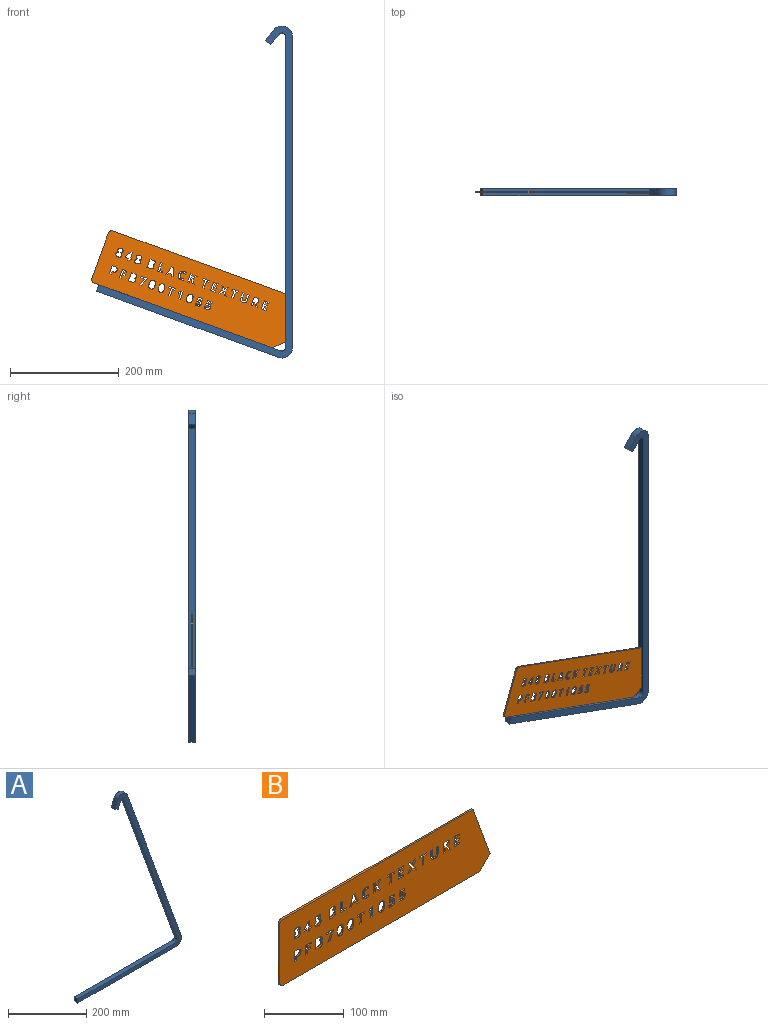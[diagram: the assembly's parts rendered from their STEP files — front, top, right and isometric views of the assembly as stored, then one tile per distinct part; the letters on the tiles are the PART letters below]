
ASSEMBLY  parts=2 mates=1
PART A: 14 faces, bbox 374.7x12.7x575.1 mm
  f0: plane 12.7x12.7mm, normal (-1,0,0), area 161.3mm2, adj f2,f3,f4,f5
  f1: plane 12.7x11.93mm, normal (-0.34,0,-0.94), area 161.3mm2, adj f3,f5,f12,f13
  f2: plane 355.6x12.7mm, normal (0,0,1), area 4516.1mm2, adj f0,f3,f5,f6
  f3: plane 575.13x374.65mm, normal (0,-1,0), area 12800.5mm2, adj f0,f1,f2,f4,f6,f7,f8,f9
  f4: plane 355.6x12.7mm, normal (0,0,-1), area 4516.1mm2, adj f0,f3,f5,f7
  f5: plane 575.13x374.65mm, normal (0,1,0), area 12800.5mm2, adj f0,f1,f2,f4,f6,f7,f8,f9
  f6: cylinder r=6.35mm len=12.7mm, axis (0,-1,0), area 154.8mm2, adj f2,f3,f5,f8
  f7: cylinder r=19.05mm len=25.57mm, axis (0,-1,0), area 464.5mm2, adj f3,f4,f5,f9
  f8: plane 537.03x195.46mm, normal (-0.94,0,-0.34), area 7258.1mm2, adj f3,f5,f6,f10
  f9: plane 537.03x195.46mm, normal (0.94,0,0.34), area 7258mm2, adj f3,f5,f7,f11
  f10: cylinder r=6.35mm len=12.7mm, axis (0,-1,0), area 197.1mm2, adj f3,f5,f8,f12
  f11: cylinder r=19.05mm len=35.8mm, axis (0,-1,0), area 591.2mm2, adj f3,f5,f9,f13
  f12: plane 23.87x12.7mm, normal (0.94,0,-0.34), area 322.6mm2, adj f1,f3,f5,f10
  f13: plane 23.87x12.7mm, normal (-0.94,0,0.34), area 322.6mm2, adj f1,f3,f5,f11
PART B: 305 faces, bbox 374.2x2.7x101.6 mm
  f0: plane 374.22x101.6mm, normal (0,-1,0), area 33695.3mm2, adj f1,f3,f4,f5,f6,f7,f8,f9
  f1: plane 337.67x2.74mm, normal (0,0,1), area 926.3mm2, adj f0,f2,f301,f303
  f2: plane 374.22x101.6mm, normal (0,1,0), area 33695.3mm2, adj f1,f3,f4,f5,f6,f7,f8,f9
  f3: plane 349.25x2.74mm, normal (0,0,-1), area 958.1mm2, adj f0,f2,f302,f304
  f4: plane 88.9x2.74mm, normal (-1,0,0), area 243.9mm2, adj f0,f2,f303,f304
  f5: plane 15.74x2.74mm, normal (1,0,0), area 43.2mm2, adj f0,f2,f6,f10
  f6: plane 9.72x2.74mm, normal (0,0,1), area 26.7mm2, adj f0,f2,f5,f7
  f7: plane 2.76x2.74mm, normal (-1,0,0), area 7.6mm2, adj f0,f2,f6,f8
  f8: plane 6.38x2.74mm, normal (0,0,-1), area 17.5mm2, adj f0,f2,f7,f9
  f9: plane 12.98x2.74mm, normal (-1,0,0), area 35.6mm2, adj f0,f2,f8,f10
  f10: plane 3.34x2.74mm, normal (0,0,-1), area 9.2mm2, adj f0,f2,f5,f9
  f11: extruded ~6.1x2.74mm, area 17.4mm2, adj f0,f2,f12,f18
  f12: extruded ~6.05x2.74mm, area 17.3mm2, adj f0,f2,f11,f13
  f13: extruded ~4.12x2.74mm, area 13.2mm2, adj f0,f2,f12,f14
  f14: extruded ~4.14x2.74mm, area 13.2mm2, adj f0,f2,f13,f15
  f15: extruded ~6.14x2.74mm, area 17.5mm2, adj f0,f2,f14,f16
  f16: extruded ~6.04x2.74mm, area 17.2mm2, adj f0,f2,f15,f17
  f17: extruded ~4.11x2.74mm, area 13.2mm2, adj f0,f2,f16,f18
  f18: extruded ~4.16x2.74mm, area 13.2mm2, adj f0,f2,f11,f17
  f19: extruded ~2.77x2.74mm, area 8.8mm2, adj f0,f2,f20,f34
  f20: extruded ~2.74x2.15mm, area 6.3mm2, adj f0,f2,f19,f21
  f21: extruded ~2.74x2.15mm, area 7.6mm2, adj f0,f2,f20,f22
  f22: extruded ~2.74x2.53mm, area 8.9mm2, adj f0,f2,f21,f23
  f23: extruded ~2.74x2.26mm, area 6.7mm2, adj f0,f2,f22,f24
  f24: extruded ~3.12x2.74mm, area 9.9mm2, adj f0,f2,f23,f25
  f25: extruded ~3.99x2.74mm, area 11.6mm2, adj f0,f2,f24,f26
  f26: extruded ~4.06x2.74mm, area 11.7mm2, adj f0,f2,f25,f27
  f27: extruded ~3.11x2.74mm, area 9.8mm2, adj f0,f2,f26,f28
  f28: extruded ~2.74x2.39mm, area 7mm2, adj f0,f2,f27,f29
  f29: extruded ~2.74x2.3mm, area 8.2mm2, adj f0,f2,f28,f30
  f30: extruded ~2.74x1.94mm, area 7.4mm2, adj f0,f2,f29,f31
  f31: extruded ~2.74x2.12mm, area 6.1mm2, adj f0,f2,f30,f32
  f32: extruded ~2.74x2.74mm, area 8.8mm2, adj f0,f2,f31,f33
  f33: extruded ~3.65x2.74mm, area 10.6mm2, adj f0,f2,f32,f34
  f34: extruded ~3.65x2.74mm, area 10.6mm2, adj f0,f2,f19,f33
  f35: extruded ~2.77x2.74mm, area 8.8mm2, adj f0,f2,f36,f50
  f36: extruded ~2.74x2.15mm, area 6.3mm2, adj f0,f2,f35,f37
  f37: extruded ~2.74x2.15mm, area 7.6mm2, adj f0,f2,f36,f38
  f38: extruded ~2.74x2.53mm, area 8.9mm2, adj f0,f2,f37,f39
  f39: extruded ~2.74x2.26mm, area 6.7mm2, adj f0,f2,f38,f40
  f40: extruded ~3.12x2.74mm, area 9.9mm2, adj f0,f2,f39,f41
  f41: extruded ~3.99x2.74mm, area 11.6mm2, adj f0,f2,f40,f42
  f42: extruded ~4.06x2.74mm, area 11.7mm2, adj f0,f2,f41,f43
  f43: extruded ~3.11x2.74mm, area 9.8mm2, adj f0,f2,f42,f44
  f44: extruded ~2.74x2.39mm, area 7mm2, adj f0,f2,f43,f45
  f45: extruded ~2.74x2.3mm, area 8.2mm2, adj f0,f2,f44,f46
  f46: extruded ~2.74x1.94mm, area 7.4mm2, adj f0,f2,f45,f47
  f47: extruded ~2.74x2.12mm, area 6.1mm2, adj f0,f2,f46,f48
  f48: extruded ~2.74x2.74mm, area 8.8mm2, adj f0,f2,f47,f49
  f49: extruded ~3.65x2.74mm, area 10.6mm2, adj f0,f2,f48,f50
  f50: extruded ~3.65x2.74mm, area 10.6mm2, adj f0,f2,f35,f49
  f51: extruded ~4.86x2.74mm, area 13.7mm2, adj f0,f2,f52,f62
  f52: extruded ~3.03x2.74mm, area 9.7mm2, adj f0,f2,f51,f53
  f53: extruded ~2.74x2.32mm, area 6.7mm2, adj f0,f2,f52,f54
  f54: extruded ~2.74x1.76mm, area 5.8mm2, adj f0,f2,f53,f55
  f55: plane 2.74x0.11mm, normal (-1,0,0), area 0.3mm2, adj f0,f2,f54,f56
  f56: extruded ~2.74x2.16mm, area 7mm2, adj f0,f2,f55,f57
  f57: extruded ~2.74x2.43mm, area 7mm2, adj f0,f2,f56,f58
  f58: extruded ~3.36x2.74mm, area 10.5mm2, adj f0,f2,f57,f59
  f59: extruded ~4.23x2.74mm, area 12.3mm2, adj f0,f2,f58,f60
  f60: plane 5.89x2.74mm, normal (0,0,1), area 16.2mm2, adj f0,f2,f59,f61
  f61: plane 15.74x2.74mm, normal (1,0,0), area 43.2mm2, adj f0,f2,f60,f62
  f62: plane 4.9x2.74mm, normal (0,0,-1), area 13.4mm2, adj f0,f2,f51,f61
  f63: plane 3.34x2.74mm, normal (0,0,1), area 9.2mm2, adj f0,f2,f64,f74
  f64: plane 15.74x2.74mm, normal (1,0,0), area 43.2mm2, adj f0,f2,f63,f65
  f65: plane 4.59x2.74mm, normal (0,0,-1), area 12.6mm2, adj f0,f2,f64,f66
  f66: extruded ~4.75x2.74mm, area 13.6mm2, adj f0,f2,f65,f67
  f67: extruded ~3.55x2.74mm, area 11mm2, adj f0,f2,f66,f68
  f68: extruded ~2.74x2.47mm, area 7.2mm2, adj f0,f2,f67,f69
  f69: extruded ~2.74x2.17mm, area 7.6mm2, adj f0,f2,f68,f70
  f70: extruded ~6.86x4.63mm, area 22.7mm2, adj f0,f2,f69,f71
  f71: plane 3.7x2.74mm, normal (0,0,1), area 10.2mm2, adj f0,f2,f70,f72
  f72: plane 6.04x3.76mm, normal (0.85,0,0.53), area 19.5mm2, adj f0,f2,f71,f73
  f73: plane 2.74x1.77mm, normal (0,0,1), area 4.9mm2, adj f0,f2,f72,f74
  f74: plane 6.04x2.74mm, normal (-1,0,0), area 16.6mm2, adj f0,f2,f63,f73
  f75: extruded ~4.52x2.74mm, area 13.2mm2, adj f0,f2,f76,f83
  f76: plane 2.74x1.43mm, normal (0,0,1), area 3.9mm2, adj f0,f2,f75,f77
  f77: plane 5.6x2.74mm, normal (-1,0,0), area 15.4mm2, adj f0,f2,f76,f78
  f78: plane 3.34x2.74mm, normal (0,0,1), area 9.2mm2, adj f0,f2,f77,f79
  f79: plane 15.74x2.74mm, normal (1,0,0), area 43.2mm2, adj f0,f2,f78,f80
  f80: plane 5.03x2.74mm, normal (0,0,-1), area 13.8mm2, adj f0,f2,f79,f81
  f81: extruded ~4.36x2.74mm, area 12.7mm2, adj f0,f2,f80,f82
  f82: extruded ~3.68x2.74mm, area 11.3mm2, adj f0,f2,f81,f83
  f83: extruded ~3.89x2.74mm, area 11.9mm2, adj f0,f2,f75,f82
  f84: extruded ~6.1x2.74mm, area 17.4mm2, adj f0,f2,f85,f91
  f85: extruded ~6.05x2.74mm, area 17.3mm2, adj f0,f2,f84,f86
  f86: extruded ~4.12x2.74mm, area 13.2mm2, adj f0,f2,f85,f87
  f87: extruded ~4.14x2.74mm, area 13.2mm2, adj f0,f2,f86,f88
  f88: extruded ~6.14x2.74mm, area 17.5mm2, adj f0,f2,f87,f89
  f89: extruded ~6.04x2.74mm, area 17.2mm2, adj f0,f2,f88,f90
  f90: extruded ~4.11x2.74mm, area 13.2mm2, adj f0,f2,f89,f91
  f91: extruded ~4.16x2.74mm, area 13.2mm2, adj f0,f2,f84,f90
  f92: extruded ~6.1x2.74mm, area 17.4mm2, adj f0,f2,f93,f99
  f93: extruded ~6.05x2.74mm, area 17.3mm2, adj f0,f2,f92,f94
  f94: extruded ~4.12x2.74mm, area 13.2mm2, adj f0,f2,f93,f95
  f95: extruded ~4.14x2.74mm, area 13.2mm2, adj f0,f2,f94,f96
  f96: extruded ~6.14x2.74mm, area 17.5mm2, adj f0,f2,f95,f97
  f97: extruded ~6.04x2.74mm, area 17.2mm2, adj f0,f2,f96,f98
  f98: extruded ~4.11x2.74mm, area 13.2mm2, adj f0,f2,f97,f99
  f99: extruded ~4.16x2.74mm, area 13.2mm2, adj f0,f2,f92,f98
  f100: extruded ~4.86x2.74mm, area 13.7mm2, adj f0,f2,f101,f111
  f101: extruded ~3.03x2.74mm, area 9.7mm2, adj f0,f2,f100,f102
  f102: extruded ~2.74x2.32mm, area 6.7mm2, adj f0,f2,f101,f103
  f103: extruded ~2.74x1.76mm, area 5.8mm2, adj f0,f2,f102,f104
  f104: plane 2.74x0.11mm, normal (-1,0,0), area 0.3mm2, adj f0,f2,f103,f105
  f105: extruded ~2.74x2.16mm, area 7mm2, adj f0,f2,f104,f106
  f106: extruded ~2.74x2.43mm, area 7mm2, adj f0,f2,f105,f107
  f107: extruded ~3.36x2.74mm, area 10.5mm2, adj f0,f2,f106,f108
  f108: extruded ~4.23x2.74mm, area 12.3mm2, adj f0,f2,f107,f109
  f109: plane 5.89x2.74mm, normal (0,0,1), area 16.2mm2, adj f0,f2,f108,f110
  f110: plane 15.74x2.74mm, normal (1,0,0), area 43.2mm2, adj f0,f2,f109,f111
  f111: plane 4.9x2.74mm, normal (0,0,-1), area 13.4mm2, adj f0,f2,f100,f110
  f112: extruded ~2.92x2.74mm, area 9.3mm2, adj f0,f2,f113,f126
  f113: extruded ~2.74x1.75mm, area 4.9mm2, adj f0,f2,f112,f114
  f114: extruded ~2.74x1.78mm, area 5.3mm2, adj f0,f2,f113,f115
  f115: plane 2.74x2.71mm, normal (-0.93,0,0.37), area 8mm2, adj f0,f2,f114,f116
  f116: extruded ~4.61x2.74mm, area 13.1mm2, adj f0,f2,f115,f117
  f117: extruded ~3.92x2.74mm, area 11.2mm2, adj f0,f2,f116,f118
  f118: extruded ~2.83x2.74mm, area 10.6mm2, adj f0,f2,f117,f119
  f119: extruded ~4.3x2.74mm, area 12.2mm2, adj f0,f2,f118,f120
  f120: extruded ~5.98x2.74mm, area 17.5mm2, adj f0,f2,f119,f121
  f121: extruded ~5.25x2.74mm, area 16mm2, adj f0,f2,f120,f122
  f122: extruded ~4.33x2.74mm, area 12.2mm2, adj f0,f2,f121,f123
  f123: plane 2.8x2.74mm, normal (-1,0,0), area 7.7mm2, adj f0,f2,f122,f124
  f124: extruded ~4.01x2.74mm, area 11.3mm2, adj f0,f2,f123,f125
  f125: extruded ~5.26x3.95mm, area 20.6mm2, adj f0,f2,f124,f126
  f126: extruded ~3.94x2.74mm, area 11.4mm2, adj f0,f2,f112,f125
  f127: plane 3.79x2.74mm, normal (0,0,1), area 10.4mm2, adj f0,f2,f128,f139
  f128: plane 8.77x5.53mm, normal (-0.85,0,-0.53), area 28.5mm2, adj f0,f2,f127,f129
  f129: plane 6.97x5.49mm, normal (-0.79,0,0.62), area 24.3mm2, adj f0,f2,f128,f130
  f130: plane 3.7x2.74mm, normal (0,0,-1), area 10.2mm2, adj f0,f2,f129,f131
  f131: plane 5.35x4.27mm, normal (0.78,0,-0.62), area 18.8mm2, adj f0,f2,f130,f132
  f132: plane 2.74x1.85mm, normal (0.82,0,-0.58), area 6.2mm2, adj f0,f2,f131,f133
  f133: plane 7.2x2.74mm, normal (-1,0,0), area 19.8mm2, adj f0,f2,f132,f134
  f134: plane 3.34x2.74mm, normal (0,0,-1), area 9.2mm2, adj f0,f2,f133,f135
  f135: plane 15.74x2.74mm, normal (1,0,0), area 43.2mm2, adj f0,f2,f134,f136
  f136: plane 3.34x2.74mm, normal (0,0,1), area 9.2mm2, adj f0,f2,f135,f137
  f137: plane 5.62x2.74mm, normal (-1,0,0), area 15.4mm2, adj f0,f2,f136,f138
  f138: plane 2.74x1.41mm, normal (-0.58,0,0.81), area 4.8mm2, adj f0,f2,f137,f139
  f139: plane 6.63x4.12mm, normal (0.85,0,0.53), area 21.4mm2, adj f0,f2,f127,f138
  f140: plane 3.34x2.74mm, normal (0,0,1), area 9.2mm2, adj f0,f2,f141,f147
  f141: plane 12.96x2.74mm, normal (-1,0,0), area 35.6mm2, adj f0,f2,f140,f142
  f142: plane 4.27x2.74mm, normal (0,0,1), area 11.7mm2, adj f0,f2,f141,f143
  f143: plane 2.78x2.74mm, normal (-1,0,0), area 7.6mm2, adj f0,f2,f142,f144
  f144: plane 11.89x2.74mm, normal (0,0,-1), area 32.6mm2, adj f0,f2,f143,f145
  f145: plane 2.78x2.74mm, normal (1,0,0), area 7.6mm2, adj f0,f2,f144,f146
  f146: plane 4.28x2.74mm, normal (0,0,1), area 11.7mm2, adj f0,f2,f145,f147
  f147: plane 12.96x2.74mm, normal (1,0,0), area 35.6mm2, adj f0,f2,f140,f146
  f148: plane 9.06x2.74mm, normal (0,0,1), area 24.9mm2, adj f0,f2,f149,f159
  f149: plane 2.76x2.74mm, normal (-1,0,0), area 7.6mm2, adj f0,f2,f148,f150
  f150: plane 5.73x2.74mm, normal (0,0,-1), area 15.7mm2, adj f0,f2,f149,f151
  f151: plane 4.06x2.74mm, normal (-1,0,0), area 11.1mm2, adj f0,f2,f150,f152
  f152: plane 5.33x2.74mm, normal (0,0,1), area 14.6mm2, adj f0,f2,f151,f153
  f153: plane 2.74x2.74mm, normal (-1,0,0), area 7.5mm2, adj f0,f2,f152,f154
  f154: plane 5.33x2.74mm, normal (0,0,-1), area 14.6mm2, adj f0,f2,f153,f155
  f155: plane 3.46x2.74mm, normal (-1,0,0), area 9.5mm2, adj f0,f2,f154,f156
  f156: plane 5.73x2.74mm, normal (0,0,1), area 15.7mm2, adj f0,f2,f155,f157
  f157: plane 2.74x2.74mm, normal (-1,0,0), area 7.5mm2, adj f0,f2,f156,f158
  f158: plane 9.06x2.74mm, normal (0,0,-1), area 24.9mm2, adj f0,f2,f157,f159
  f159: plane 15.74x2.74mm, normal (1,0,0), area 43.2mm2, adj f0,f2,f148,f158
  f160: plane 3.81x2.74mm, normal (0,0,1), area 10.5mm2, adj f0,f2,f161,f171
  f161: plane 7.93x5.32mm, normal (-0.83,0,-0.56), area 26.2mm2, adj f0,f2,f160,f162
  f162: plane 7.81x4.94mm, normal (-0.85,0,0.53), area 25.3mm2, adj f0,f2,f161,f163
  f163: plane 3.59x2.74mm, normal (0,0,-1), area 9.9mm2, adj f0,f2,f162,f164
  f164: plane 5.66x3.33mm, normal (0.86,0,-0.51), area 18mm2, adj f0,f2,f163,f165
  f165: plane 5.66x3.39mm, normal (-0.86,0,-0.51), area 18.1mm2, adj f0,f2,f164,f166
  f166: plane 3.68x2.74mm, normal (0,0,-1), area 10.1mm2, adj f0,f2,f165,f167
  f167: plane 7.62x4.89mm, normal (0.84,0,0.54), area 24.8mm2, adj f0,f2,f166,f168
  f168: plane 8.12x5.22mm, normal (0.84,0,-0.54), area 26.5mm2, adj f0,f2,f167,f169
  f169: plane 3.58x2.74mm, normal (0,0,1), area 9.8mm2, adj f0,f2,f168,f170
  f170: plane 5.95x3.66mm, normal (-0.85,0,0.52), area 19.2mm2, adj f0,f2,f169,f171
  f171: plane 5.95x3.66mm, normal (0.85,0,0.52), area 19.2mm2, adj f0,f2,f160,f170
  f172: plane 3.34x2.74mm, normal (0,0,1), area 9.2mm2, adj f0,f2,f173,f179
  f173: plane 12.96x2.74mm, normal (-1,0,0), area 35.6mm2, adj f0,f2,f172,f174
  f174: plane 4.27x2.74mm, normal (0,0,1), area 11.7mm2, adj f0,f2,f173,f175
  f175: plane 2.78x2.74mm, normal (-1,0,0), area 7.6mm2, adj f0,f2,f174,f176
  f176: plane 11.89x2.74mm, normal (0,0,-1), area 32.6mm2, adj f0,f2,f175,f177
  f177: plane 2.78x2.74mm, normal (1,0,0), area 7.6mm2, adj f0,f2,f176,f178
  f178: plane 4.28x2.74mm, normal (0,0,1), area 11.7mm2, adj f0,f2,f177,f179
  f179: plane 12.96x2.74mm, normal (1,0,0), area 35.6mm2, adj f0,f2,f172,f178
  f180: plane 10.18x2.74mm, normal (-1,0,0), area 27.9mm2, adj f0,f2,f181,f194
  f181: plane 3.33x2.74mm, normal (0,0,-1), area 9.1mm2, adj f0,f2,f180,f182
  f182: plane 9.62x2.74mm, normal (1,0,0), area 26.4mm2, adj f0,f2,f181,f183
  f183: extruded ~2.74x2.69mm, area 7.8mm2, adj f0,f2,f182,f184
  f184: extruded ~2.74x2.37mm, area 7.1mm2, adj f0,f2,f183,f185
  f185: extruded ~2.74x2.42mm, area 7.3mm2, adj f0,f2,f184,f186
  f186: extruded ~2.74x2.67mm, area 7.8mm2, adj f0,f2,f185,f187
  f187: plane 9.64x2.74mm, normal (-1,0,0), area 26.4mm2, adj f0,f2,f186,f188
  f188: plane 3.32x2.74mm, normal (0,0,-1), area 9.1mm2, adj f0,f2,f187,f189
  f189: plane 10.14x2.74mm, normal (1,0,0), area 27.8mm2, adj f0,f2,f188,f190
  f190: extruded ~4.26x2.74mm, area 12.9mm2, adj f0,f2,f189,f191
  f191: extruded ~4.71x2.74mm, area 14mm2, adj f0,f2,f190,f192
  f192: extruded ~3.49x2.74mm, area 9.8mm2, adj f0,f2,f191,f193
  f193: extruded ~2.74x2.26mm, area 8.4mm2, adj f0,f2,f192,f194
  f194: extruded ~3.06x2.74mm, area 8.8mm2, adj f0,f2,f180,f193
  f195: plane 9.06x2.74mm, normal (0,0,1), area 24.9mm2, adj f0,f2,f196,f206
  f196: plane 2.76x2.74mm, normal (-1,0,0), area 7.6mm2, adj f0,f2,f195,f197
  f197: plane 5.73x2.74mm, normal (0,0,-1), area 15.7mm2, adj f0,f2,f196,f198
  f198: plane 4.06x2.74mm, normal (-1,0,0), area 11.1mm2, adj f0,f2,f197,f199
  f199: plane 5.33x2.74mm, normal (0,0,1), area 14.6mm2, adj f0,f2,f198,f200
  f200: plane 2.74x2.74mm, normal (-1,0,0), area 7.5mm2, adj f0,f2,f199,f201
  f201: plane 5.33x2.74mm, normal (0,0,-1), area 14.6mm2, adj f0,f2,f200,f202
  f202: plane 3.46x2.74mm, normal (-1,0,0), area 9.5mm2, adj f0,f2,f201,f203
  f203: plane 5.73x2.74mm, normal (0,0,1), area 15.7mm2, adj f0,f2,f202,f204
  f204: plane 2.74x2.74mm, normal (-1,0,0), area 7.5mm2, adj f0,f2,f203,f205
  f205: plane 9.06x2.74mm, normal (0,0,-1), area 24.9mm2, adj f0,f2,f204,f206
  f206: plane 15.74x2.74mm, normal (1,0,0), area 43.2mm2, adj f0,f2,f195,f205
  f207: plane 3.75x2.74mm, normal (0.96,0,0.29), area 10.7mm2, adj f0,f2,f208,f214
  f208: plane 3.6x2.74mm, normal (0,0,1), area 9.9mm2, adj f0,f2,f207,f209
  f209: plane 15.81x5.58mm, normal (-0.94,0,-0.33), area 46mm2, adj f0,f2,f208,f210
  f210: plane 4.08x2.74mm, normal (0,0,-1), area 11.2mm2, adj f0,f2,f209,f211
  f211: plane 15.81x5.56mm, normal (0.94,0,-0.33), area 46mm2, adj f0,f2,f210,f212
  f212: plane 3.6x2.74mm, normal (0,0,1), area 9.9mm2, adj f0,f2,f211,f213
  f213: plane 3.75x2.74mm, normal (-0.96,0,0.29), area 10.7mm2, adj f0,f2,f212,f214
  f214: plane 5.74x2.74mm, normal (0,0,1), area 15.7mm2, adj f0,f2,f207,f213
  f215: plane 2.74x1.9mm, normal (0,0,1), area 5.2mm2, adj f0,f2,f216,f225
  f216: plane 2.74x2.58mm, normal (-1,0,0), area 7.1mm2, adj f0,f2,f215,f217
  f217: plane 2.74x1.9mm, normal (0,0,-1), area 5.2mm2, adj f0,f2,f216,f218
  f218: plane 9.89x2.74mm, normal (-1,0,0), area 27.1mm2, adj f0,f2,f217,f219
  f219: plane 3.07x2.74mm, normal (0,0,-1), area 8.4mm2, adj f0,f2,f218,f220
  f220: plane 10.16x6.9mm, normal (0.83,0,-0.56), area 33.7mm2, adj f0,f2,f219,f221
  f221: plane 2.74x2.32mm, normal (1,0,0), area 6.4mm2, adj f0,f2,f220,f222
  f222: plane 6.72x2.74mm, normal (0,0,1), area 18.4mm2, adj f0,f2,f221,f223
  f223: plane 3.26x2.74mm, normal (1,0,0), area 8.9mm2, adj f0,f2,f222,f224
  f224: plane 3.25x2.74mm, normal (0,0,1), area 8.9mm2, adj f0,f2,f223,f225
  f225: plane 3.26x2.74mm, normal (-1,0,0), area 8.9mm2, adj f0,f2,f215,f224
  f226: extruded ~3.63x2.74mm, area 10.8mm2, adj f0,f2,f227,f245
  f227: extruded ~2.74x1.63mm, area 4.5mm2, adj f0,f2,f226,f228
  f228: plane 2.74x0.38mm, normal (0.2,0,-0.98), area 1.1mm2, adj f0,f2,f227,f229
  f229: plane 3.09x2.74mm, normal (-1,0,0.09), area 8.5mm2, adj f0,f2,f228,f230
  f230: plane 5.62x2.74mm, normal (0,0,1), area 15.4mm2, adj f0,f2,f229,f231
  f231: plane 2.82x2.74mm, normal (-1,0,0), area 7.7mm2, adj f0,f2,f230,f232
  f232: plane 8.54x2.74mm, normal (0,0,-1), area 23.4mm2, adj f0,f2,f231,f233
  f233: plane 8.02x2.74mm, normal (1,0,-0.07), area 22.1mm2, adj f0,f2,f232,f234
  f234: plane 2.74x1.33mm, normal (0.47,0,0.88), area 4.1mm2, adj f0,f2,f233,f235
  f235: extruded ~2.74x1.12mm, area 3.1mm2, adj f0,f2,f234,f236
  f236: extruded ~2.74x1.26mm, area 3.5mm2, adj f0,f2,f235,f237
  f237: extruded ~3.16x2.74mm, area 12.4mm2, adj f0,f2,f236,f238
  f238: extruded ~3.05x2.74mm, area 12.4mm2, adj f0,f2,f237,f239
  f239: extruded ~2.74x2.14mm, area 5.9mm2, adj f0,f2,f238,f240
  f240: extruded ~2.74x1.98mm, area 5.8mm2, adj f0,f2,f239,f241
  f241: plane 2.88x2.74mm, normal (1,0,0), area 7.9mm2, adj f0,f2,f240,f242
  f242: extruded ~4.24x2.74mm, area 12mm2, adj f0,f2,f241,f243
  f243: extruded ~4.65x2.74mm, area 13.6mm2, adj f0,f2,f242,f244
  f244: extruded ~4.06x2.74mm, area 12.4mm2, adj f0,f2,f243,f245
  f245: extruded ~3.51x2.74mm, area 10.6mm2, adj f0,f2,f226,f244
  f246: extruded ~3.63x2.74mm, area 10.8mm2, adj f0,f2,f247,f265
  f247: extruded ~2.74x1.63mm, area 4.5mm2, adj f0,f2,f246,f248
  f248: plane 2.74x0.38mm, normal (0.2,0,-0.98), area 1.1mm2, adj f0,f2,f247,f249
  f249: plane 3.09x2.74mm, normal (-1,0,0.09), area 8.5mm2, adj f0,f2,f248,f250
  f250: plane 5.62x2.74mm, normal (0,0,1), area 15.4mm2, adj f0,f2,f249,f251
  f251: plane 2.82x2.74mm, normal (-1,0,0), area 7.7mm2, adj f0,f2,f250,f252
  f252: plane 8.54x2.74mm, normal (0,0,-1), area 23.4mm2, adj f0,f2,f251,f253
  f253: plane 8.02x2.74mm, normal (1,0,-0.07), area 22.1mm2, adj f0,f2,f252,f254
  f254: plane 2.74x1.33mm, normal (0.47,0,0.88), area 4.1mm2, adj f0,f2,f253,f255
  f255: extruded ~2.74x1.12mm, area 3.1mm2, adj f0,f2,f254,f256
  f256: extruded ~2.74x1.26mm, area 3.5mm2, adj f0,f2,f255,f257
  f257: extruded ~3.16x2.74mm, area 12.4mm2, adj f0,f2,f256,f258
  f258: extruded ~3.05x2.74mm, area 12.4mm2, adj f0,f2,f257,f259
  f259: extruded ~2.74x2.14mm, area 5.9mm2, adj f0,f2,f258,f260
  f260: extruded ~2.74x1.98mm, area 5.8mm2, adj f0,f2,f259,f261
  f261: plane 2.88x2.74mm, normal (1,0,0), area 7.9mm2, adj f0,f2,f260,f262
  f262: extruded ~4.24x2.74mm, area 12mm2, adj f0,f2,f261,f263
  f263: extruded ~4.65x2.74mm, area 13.6mm2, adj f0,f2,f262,f264
  f264: extruded ~4.06x2.74mm, area 12.4mm2, adj f0,f2,f263,f265
  f265: extruded ~3.51x2.74mm, area 10.6mm2, adj f0,f2,f246,f264
  f266: plane 3.33x2.74mm, normal (0,0,1), area 9.1mm2, adj f0,f2,f267,f275
  f267: plane 15.74x2.74mm, normal (-1,0,0), area 43.2mm2, adj f0,f2,f266,f268
  f268: plane 2.74x2.74mm, normal (0,0,-1), area 7.5mm2, adj f0,f2,f267,f269
  f269: plane 5.07x4.04mm, normal (0.62,0,-0.78), area 17.8mm2, adj f0,f2,f268,f270
  f270: plane 2.74x2mm, normal (0.78,0,0.63), area 7mm2, adj f0,f2,f269,f271
  f271: plane 2.74x1.81mm, normal (-0.63,0,0.78), area 6.4mm2, adj f0,f2,f270,f272
  f272: extruded ~2.74x1.15mm, area 4.3mm2, adj f0,f2,f271,f273
  f273: plane 2.74x1.64mm, normal (1,0,-0.03), area 4.5mm2, adj f0,f2,f272,f274
  f274: plane 2.74x1.5mm, normal (1,0,-0.02), area 4.1mm2, adj f0,f2,f273,f275
  f275: plane 9.11x2.74mm, normal (1,0,0), area 25mm2, adj f0,f2,f266,f274
  f276: plane 3.34x2.74mm, normal (0,0,1), area 9.2mm2, adj f0,f2,f277,f283
  f277: plane 12.96x2.74mm, normal (-1,0,0), area 35.6mm2, adj f0,f2,f276,f278
  f278: plane 4.27x2.74mm, normal (0,0,1), area 11.7mm2, adj f0,f2,f277,f279
  f279: plane 2.78x2.74mm, normal (-1,0,0), area 7.6mm2, adj f0,f2,f278,f280
  f280: plane 11.89x2.74mm, normal (0,0,-1), area 32.6mm2, adj f0,f2,f279,f281
  f281: plane 2.78x2.74mm, normal (1,0,0), area 7.6mm2, adj f0,f2,f280,f282
  f282: plane 4.28x2.74mm, normal (0,0,1), area 11.7mm2, adj f0,f2,f281,f283
  f283: plane 12.96x2.74mm, normal (1,0,0), area 35.6mm2, adj f0,f2,f276,f282
  f284: plane 12.92x5.91mm, normal (0.91,0,-0.42), area 39mm2, adj f0,f2,f285,f290
  f285: plane 3.49x2.74mm, normal (0,0,1), area 9.6mm2, adj f0,f2,f284,f286
  f286: plane 13.63x5.95mm, normal (-0.92,0,0.4), area 40.8mm2, adj f0,f2,f285,f287
  f287: plane 2.74x2.09mm, normal (-1,0,0), area 5.7mm2, adj f0,f2,f286,f288
  f288: plane 11.29x2.74mm, normal (0,0,-1), area 31mm2, adj f0,f2,f287,f289
  f289: plane 2.8x2.74mm, normal (1,0,0), area 7.7mm2, adj f0,f2,f288,f290
  f290: plane 7.76x2.74mm, normal (0,0,1), area 21.3mm2, adj f0,f2,f284,f289
  f291: plane 3.28x2.74mm, normal (0,0,1), area 9mm2, adj f0,f2,f292,f300
  f292: plane 6.22x2.74mm, normal (-1,0,0), area 17.1mm2, adj f0,f2,f291,f293
  f293: plane 5.34x2.74mm, normal (0,0,1), area 14.6mm2, adj f0,f2,f292,f294
  f294: plane 2.74x2.73mm, normal (-1,0,0), area 7.5mm2, adj f0,f2,f293,f295
  f295: plane 5.34x2.74mm, normal (0,0,-1), area 14.6mm2, adj f0,f2,f294,f296
  f296: plane 4.06x2.74mm, normal (-1,0,0), area 11.1mm2, adj f0,f2,f295,f297
  f297: plane 5.74x2.74mm, normal (0,0,1), area 15.7mm2, adj f0,f2,f296,f298
  f298: plane 2.74x2.74mm, normal (-1,0,0), area 7.5mm2, adj f0,f2,f297,f299
  f299: plane 9.02x2.74mm, normal (0,0,-1), area 24.8mm2, adj f0,f2,f298,f300
  f300: plane 15.74x2.74mm, normal (1,0,0), area 43.2mm2, adj f0,f2,f291,f299
  f301: plane 82.98x30.2mm, normal (0.94,0,0.34), area 242.2mm2, adj f0,f1,f2,f302
  f302: plane 18.62x18.62mm, normal (0.71,0,-0.71), area 72.2mm2, adj f0,f2,f3,f301
  f303: cylinder r=6.35mm len=6.35mm, axis (0,1,0), area 27.4mm2, adj f0,f1,f2,f4
  f304: cylinder r=6.35mm len=6.35mm, axis (0,-1,0), area 27.4mm2, adj f0,f2,f3,f4
PLACE A rot(axis=(0,1,0),20deg) t=(-344.85,6.35,-461.81)mm
PLACE B rot(axis=(0,1,0),20deg) t=(35.18,7.72,-485.25)mm
MATE fastened B.f3 <-> A.f2  axis (0.34,0,0.94) through (-23.44,6.35,-572.04)mm
